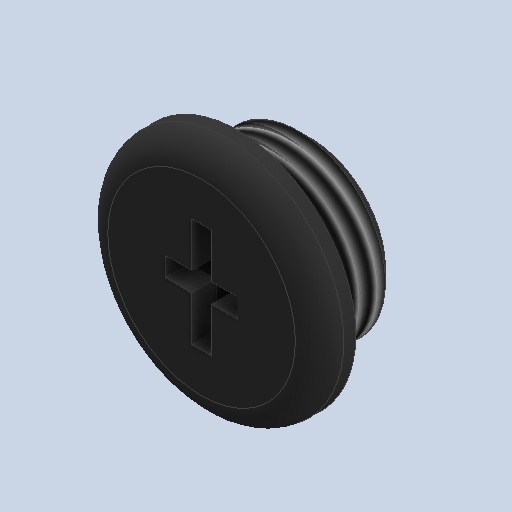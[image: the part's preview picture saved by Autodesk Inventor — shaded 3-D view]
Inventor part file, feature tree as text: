
AUTODESK INVENTOR PART (.ipt)
format: ipt  version: 2024.2 (Build 282272000, 272)  size: 189,952 bytes
history: native  units: mm
features: extrude x3, fillet x1, thread x1, chamfer x1, sketch x1
ambient origin geometry x8: Origin, YZ Plane, XZ Plane, XY Plane, X Axis, Y Axis, Z Axis, Center Point
bodies: Solid1 (feature_tree)
feature tree (7):
  extrude  "Extrusion1"  Depth=3.0mm TaperAngle=0.0deg
  extrude  "Extrusion2"  Depth=2.0mm
  fillet  "Fillet1"  Radius=2.5mm
  extrude  "Extrusion3"  Depth=6.0mm TaperAngle=0.0deg
  thread  "Thread1"  [1 undecoded]
  chamfer  "Chamfer1"  Distance=9.0mm
  sketch  "Sketch3"  dims[d0=19.5mm d1=3.0mm d2=0.0mm d3=14.4mm d4=2.5mm d5=6.0mm d6=0.0mm d7=2.0mm d8=9.0mm d9=6.0mm d10=1.6mm d11=1.6mm d12=2.0mm d13=0.0mm d14=6.0mm d15=0.0mm d16=1.0mm d17=2.0mm d18=45.0deg]
note: 1 required parameter value undecoded (feature->parameter linkage not recoverable at this tier; creation-order binding heuristic only, values carry confidence <= 0.55)
